# Revit family: WashBasin-40cm-BowlCounterTop-Vitra-WaterJewelsSeries-4334
name_source: partatom
category: Plumbing Fixtures
revit_build: Autodesk Revit 2017 (Build: 20160225_1515(x64)
units: mm (PartAtom-declared; Revit-internal decimal feet)

## family parameters
Cut with Voids When Loaded = No
Host = Face
OmniClass Number = 23.45.05.14.14
OmniClass Title = Sinks/Lavatories
Part Type = Normal
Room Calculation Point = No
Round Connector Dimension = Use Diameter
Shared = Yes

## types (20) — shared parameters
BIMobject category = Sanitary - Basins
Brand = VitrA
CW Connection = No
Default Elevation = 850 mm
Design country = Turkey
HW Connection = No
IFC Classification = Sanitary Terminal
Main Material = Ceramic
Manufacturer = VitrA
Masterformat 2014 Code = 22 41 16
Masterformat 2014 Description = Residential Lavatories and Sinks
Mounting type = Countertop
NBS Referans Code = 35-65-70-94
NBS Referans Description = Wash Basin Systems
Nominal Depth (mm) = 400 mm  [stored 1.31234 ft]
Nominal Height (mm) = 140 mm  [stored 0.459318 ft]
Nominal Width (mm) = 400 mm  [stored 1.31234 ft]
OmniClass Code = 23.45.05.14.14
OmniClass Description = Sinks/Lavatories
Product Guid = https://cdn.vitra.com.tr
Product family = Counter Top Washbasins
Product group = Water Jewels
UNSPSC Code = 301815
Uniclass 1.4 Code = L7212
Uniclass 1.4 Description = Washbasins
Uniclass 2.0 Code = SS-35-65-70-94
Uniclass 2.0 Description = Sanitary Dispensing And Disposal Units
Uniclass 2015 Code = Pr_40_20_96_81
Uniclass 2015 Name = Wash basins Sinks and troughs
Uniformat II Code = D2010
Uniformat II Description = Plumbing Fixtures
Vent Connection = No
Warranty Period (Year) = 10 Years
Youtube = https://www.youtube.com

## per-type parameters (varying)
| type | Article No. (default) | Color | Description | Manufacturer name | Model | Primary Material | Product SKU | Product certification | Product data url | Product url | Secondary Material | Technical description | Third Material | Waste Connection | Weight Net (kg) |
| WashBasin(CounterTop)-Vitra_WaterJewelsSeries(Black-White)_4334B097-1747 | 4334B097-1747 | Black & White | VitrA WaterJewelsSeries Bowl 40cm | Vitra | 4334B097-1747 | Black | 4334B097-1747 | https://www.vitra.com.tr | https://www.vitraglobal.com |  | White | https://www.vitraglobal.com | Black | Yes | 6.8 |
| WashBasin(CounterTop)-Vitra_WaterJewelsSeries(CopperPatterned)_4334B073-2100 | 4334B073-2100 | Copper Patterned | VitrA WaterJewelsSeries Bowl 40cm | Vitra | 4334B073-2100 | Copper | 4334B073-2100 | https://www.vitra.com.tr | https://www.vitraglobal.com |  | Copper | https://www.vitraglobal.com | Copper | Yes | 6.8 |
| WashBasin(CounterTop)-Vitra_WaterJewelsSeries(Copper)_4334B073-0016 | 4334B073-0016 | Copper | VitrA WaterJewelsSeries Bowl 40cm | Vitra | 4334B073-0016 | Copper | 4334B073-0016 | https://www.vitra.com.tr | https://www.vitraglobal.com |  | Copper | https://www.vitraglobal.com | Copper | Yes | 6.8 |
| WashBasin(CounterTop)-Vitra_WaterJewelsSeries(Gold-Patterned)_4334B072-2100 | 4334B072-2100 | Gold Patterned | VitrA WaterJewelsSeries Bowl 40cm | Vitra | 4334B072-2100 | Gold | 4334B072-2100 | https://www.vitra.com.tr | https://www.vitraglobal.com |  | Gold | https://www.vitraglobal.com | Gold | No | 6.8 |
| WashBasin(CounterTop)-Vitra_WaterJewelsSeries(Gold)_4334B072-0016 | 4334B072-0016 | Gold | VitrA WaterJewelsSeries Bowl 40cm | Vitra | 4334B072-0016 | Gold | 4334B072-0016 | https://www.vitra.com.tr | https://www.vitraglobal.com |  | Gold | https://www.vitraglobal.com | Gold | Yes | 6.8 |
| WashBasin(CounterTop)-Vitra_WaterJewelsSeries(Platinum-Patterned)_4334B071-2100 | 4334B071-2100 | Platinum Patterned | VitrA WaterJewelsSeries Bowl 40cm | Vitra | 4334B071-2100 | Platinum | 4334B071-2100 | https://www.vitra.com.tr | https://www.vitraglobal.com |  | Platinum | https://www.vitraglobal.com | Platinum | Yes | 6.8 |
| WashBasin(CounterTop)-Vitra_WaterJewelsSeries(Platinum)_4334B071-0016 | 4334B071-0016 | Platinum | VitrA WaterJewelsSeries Bowl 40cm | Vitra | 4334B071-0016 | Platinum | 4334B071-0016 | https://www.vitraglobal.com | https://www.vitraglobal.com |  | Platinum | https://www.vitraglobal.com | White | Yes | 6.8 |
| WashBasin(CounterTop)-Vitra_WaterJewelsSeries(Black)_4334B070-0016 | 4334B070-0016 | Black | VitrA WaterJewelsSeries Bowl 40cm | Vitra | 4334B070-0016 | Black | 4334B070-0016 | https://www.vitra.com.tr | https://www.vitraglobal.com |  | Black | https://www.vitraglobal.com | Black | Yes | 6.8 |
| WashBasin(CounterTop)-Vitra_WaterJewelsSeries(Terracota-Turquise)_4334B049-0016 | 4334B049-0016 | Terracota-Turquies | VitrA WaterJewelsSeries Bowl 40cm | Vitra | 4334B049-0016 | Terrarosa | 4334B049-0016 | https://www.vitra.com.tr | https://www.vitraglobal.com |  | Turquies | https://www.vitraglobal.com | Terrarosa | Yes | 6.8 |
| WashBasin(CounterTop)-Vitra_WaterJewelsSeries(Terracota-Blue)_4334B043-0016 | 4334B043-0016 | Terracota-Blue | VitrA WaterJewelsSeries Bowl 40cm | Vitra | 4334B043-0016 | Terrarosa | 4334B043-0016 | https://www.vitra.com.tr | https://www.vitraglobal.com |  | Blue | https://www.vitraglobal.com | Terrarosa | Yes | 6.8 |
| WashBasin(CounterTop)-Vitra_WaterJewelsSeries(White)_4334B003-1361 | 4334B003-1361 | White | VitrA WaterJewelsSeries Bowl 40cm | Vitra | 4334B003-1361 | White | 4334B003-1361 | https://www.vitra.com.tr | https://www.vitraglobal.com |  | White | https://www.vitraglobal.com | White | Yes | 6.8 |
| WashBasin(CounterTop)-Vitra_WaterJewelsSeries(White)_4334B003H1361 | 4334B003H1361 | White | VitrA WaterJewelsSeries Bowl 40cm | Vitra | 4334B003H1361 | White | 4334B003H1361 | https://www.vitra.com.tr |  | https://www.vitra-india.com | White | https://www.vitra-india.com | White | Yes | 6.8 |
| WashBasin(CounterTop)-Vitra_WaterJewelsSeries(Black)_4334B070H0016 | 4334B070H0016 | Black | VitrA WaterJewelsSeries Bowl 40cm | Vitra | 4334B070H0016 | Black | 4334B070H0016 | https://www.vitra.com.tr |  | https://www.vitra-india.com | Black | https://www.vitra-india.com | Black | Yes | 6.8 |
| WashBasin(CounterTop)-Vitra_WaterJewelsSeries(Platinum)_4334B071H0016 | 4334B071H0016 | Platinum | VitrA WaterJewelsSeries Bowl 40cm | Vitra | 4334B071H0016 | Platinum | 4334B071H0016 | https://www.vitraglobal.com |  | https://www.vitra-india.com | Platinum | https://www.vitra-india.com | White | Yes | 6.8 |
| WashBasin(CounterTop)-Vitra_WaterJewelsSeries(Gold)_4334B072H0016 | 4334B072H0016 | Gold | VitrA WaterJewelsSeries Bowl 40cm | Vitra | 4334B072H0016 | Gold | 4334B072H0016 | https://www.vitra.com.tr |  | https://www.vitra-india.com | Gold | https://www.vitra-india.com | Gold | Yes | 6.8 |
| WashBasin(CounterTop)-Vitra_WaterJewelsSeries(Copper)_4334B073H0016 | 4334B073H0016 | Copper | VitrA WaterJewelsSeries Bowl 40cm | Vitra | 4334B073H0016 | Copper | 4334B073H0016 | https://www.vitra.com.tr |  | https://www.vitra-india.com | Copper | https://www.vitra-india.com | Copper | Yes | 6.8 |
| WashBasin(CounterTop)-Vitra_WaterJewelsSeries(White)_4334B071H2300 | 4334B071H2300 | White | VitrA WaterJewelsSeries Bowl 40cm | Vitra | 4334B071H2300 | Platinum | 4334B071H2300 | https://www.vitra.com.tr |  | https://www.vitra-india.com | White | https://www.vitra-india.com | White | Yes | 6.8 |
| WashBasin(CounterTop)-Vitra_WaterJewelsSeries(White)_4334B072H2300 | 4334B072H2300 | White | VitrA WaterJewelsSeries Bowl 40cm | Vitra | 4334B072H2300 | Gold | 4334B072H2300 | https://www.vitra.com.tr |  | https://www.vitra-india.com | White | https://www.vitra-india.com | White | Yes | 6.8 |
| WashBasin(CounterTop)-Vitra_WaterJewelsSeries(White)_4334B073H2300 | 4334B073H2300 | White | VitrA WaterJewelsSeries Bowl 40cm | Vitra | 4334B073H2300 | Copper | 4334B073H2300 | https://www.vitra.com.tr |  | https://www.vitra-india.com | White | https://www.vitra-india.com | White | Yes | 6.8 |
| WashBasin(CounterTop)-Vitra_WaterJewelsSeries(Terrarosa-Blue) VC_4334B426-0016 | 4334B426-0016 | Terrarosa Blue | VitrA -WaterJewelsSeries- VitrA Clean- Bowl-40cm | VitrA | 4334B426-0016 | Terrarosa | 4334B426-0016 | https://www.vitra.com.tr | https://www.vitraglobal.com |  | Blue | https://www.vitraglobal.com | Terrarosa | Yes | 7 |

note: [stored X ft] marks values corroborated as IEEE doubles in the binary element streams (Revit-internal decimal feet)

## geometry (parser evidence)
native form markers: Sweep x3
no freeform markers — native parametric forms only
